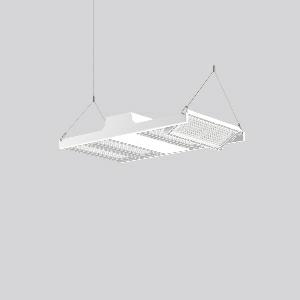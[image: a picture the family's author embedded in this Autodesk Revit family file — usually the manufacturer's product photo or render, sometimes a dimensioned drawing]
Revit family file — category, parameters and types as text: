
# Revit family: light_case_921687_002_1_76_d487
name_source: partatom
category: Lighting Fixtures
units: mm (PartAtom-declared; Revit-internal decimal feet)

## family parameters
Cut with Voids When Loaded = No
Host = Face
Light Source = No
Part Type = Normal
Room Calculation Point = No
Round Connector Dimension = Use Diameter
Shared = No

## types (1)
- LIGHT CASE (1 x LED Modul 865, 8700 lm, 6500)
    Apparent Load = 225 VA
    CIE Flux Codes = 85 97 100 100 100
    Color Rendering = 80
    Color Temperature = 6500
    Default Elevation = 1800 mm
    Description = Series: LIGHT CASE
Flat highbay luminaire for chain or cable suspension with 4 LED modules that can be swivelled. Housing: die cast aluminium and sheet steel, powder-coated. Optimised thermal management thanks to special luminaire design. Self-cleaning heat sink for constant heat dissipation. Cover: plastic (polycarbonate, shockproof), with integrated four-row lens system. LED modules can be swivelled ± 30° for optimum illumination. Suitable for chain or steel cable suspension (to be provided on site). With 5-pin connection terminal (1.5 m). With integrated movement sensor and light sensor for daylight detection on request. Ball impact proof in accordance with DIN 18032-03 (except steel cable suspension). Luminaire with limited surface temperature in accordance with EN 60598-2-24 for use in environments in which a deposit of conductive dust on the luminaire can be expected. 
Colour: white
Length: 680 mm
Width: 397 mm
Height: 110 mm
Lamp: LED
Socket: without socket
Colour temperature: 6500K
Colour rendering index (CRI): 80
System power: 225 W
Rated luminous flux: 34800 lm
Luminous efficiency: 155 lm/W
Control gear: Converter, dimmable, DALI
Protection class: I
Type of protection: IP 65
    Height = 110 mm
    Lamp = 1 x LED Modul 865
    Lamp Light Flux = 8700 lm
    Lamp count = 1
    Length = 680 mm
    Lifetime = 50000 h
    Luminous efficacy = 155 lm/W
    Manufacturer = RZB
    ModVariant = No
    Model = 921687.002.1.76
    Mounting Place = Ceiling
    Mounting Type = Pendant
    Number of Poles = 1
    OnlyDefault = Yes
    Power Factor = 1
    Product Name = LIGHT CASE
    Product group = Pendant commercial luminaires
    ProductGroupID = 903
    Protection Class = Protection class I
    Protection Degree = IP 65
    RLX_Detail_Level = 1
    RLX_Emergency_Light_Flux = 0 lm
    RLX_Emergency_Type = 0
    RLX_Emergency_Type_DB = No
    RlxData = <blob elided: 28153 chars, md5=ac8295ee>
    Socket = socket
    Standby Power = 0 W
    System Light Flux = 34800 lm
    System Power = 225 W
    Type Comments = Product without accessories
    Type Image = 921523.002.76.jpg
    URL = http://relux.com
    VarID = ---
    Voltage = 230 V
    Voltage Range = 220-240 V
    Weight = 0.00 kg
    Width = 397 mm

## geometry (parser evidence)
native form markers: Blend x4, Sweep x18
no freeform markers — native parametric forms only
